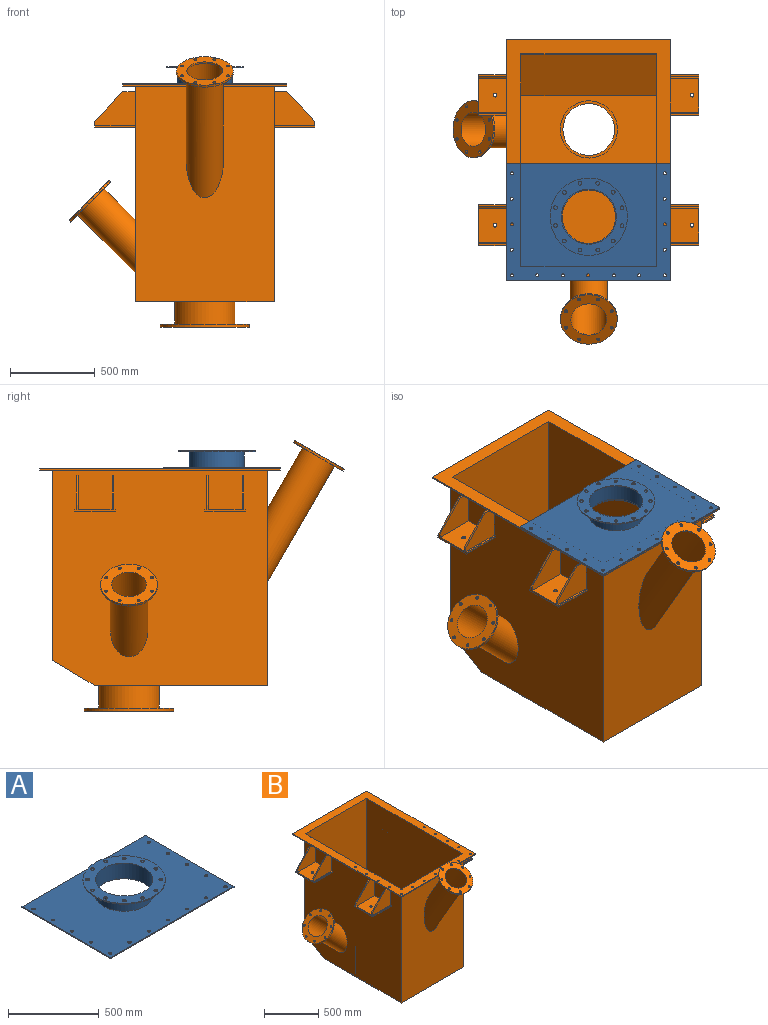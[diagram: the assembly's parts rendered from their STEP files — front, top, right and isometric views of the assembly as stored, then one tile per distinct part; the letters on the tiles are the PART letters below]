
ASSEMBLY  parts=2 mates=1
PART A: 38 faces, bbox 966x690x106 mm
  f0: cylinder r=161.9mm len=323.8mm, axis (0,0,-1), area 95621.3mm2, adj f20,f35
  f1: plane 966x6mm, normal (0,1,0), area 5796mm2, adj f2,f18,f20,f21
  f2: plane 690x6mm, normal (-1,0,0), area 4140mm2, adj f1,f3,f20,f21
  f3: plane 966x6mm, normal (0,-1,0), area 5796mm2, adj f2,f18,f20,f21
  f4: cylinder r=9mm len=18mm, axis (0,0,-1), area 339.3mm2, adj f20,f21
  f5: cylinder r=9mm len=18mm, axis (0,0,-1), area 339.3mm2, adj f20,f21
  f6: cylinder r=9mm len=18mm, axis (0,0,-1), area 339.3mm2, adj f20,f21
  f7: cylinder r=9mm len=18mm, axis (0,0,-1), area 339.3mm2, adj f20,f21
  f8: cylinder r=9mm len=18mm, axis (0,0,-1), area 339.3mm2, adj f20,f21
  f9: cylinder r=9mm len=18mm, axis (0,0,-1), area 339.3mm2, adj f20,f21
  f10: cylinder r=9mm len=18mm, axis (0,0,-1), area 339.3mm2, adj f20,f21
  f11: cylinder r=9mm len=18mm, axis (0,0,-1), area 339.3mm2, adj f20,f21
  f12: cylinder r=9mm len=18mm, axis (0,0,-1), area 339.3mm2, adj f20,f21
  f13: cylinder r=9mm len=18mm, axis (0,0,-1), area 339.3mm2, adj f20,f21
  f14: cylinder r=9mm len=18mm, axis (0,0,-1), area 339.3mm2, adj f20,f21
  f15: cylinder r=9mm len=18mm, axis (0,0,-1), area 339.3mm2, adj f20,f21
  f16: cylinder r=9mm len=18mm, axis (0,0,-1), area 339.3mm2, adj f20,f21
  f17: cylinder r=9mm len=18mm, axis (0,0,-1), area 339.3mm2, adj f20,f21
  f18: plane 690x6mm, normal (1,0,0), area 4140mm2, adj f1,f3,f20,f21
  f19: cylinder r=9mm len=18mm, axis (0,0,-1), area 339.3mm2, adj f20,f21
  f20: plane 966x690mm, normal (0,0,1), area 580376.8mm2, adj f0,f1,f2,f3,f4,f5,f6,f7
  f21: plane 966x690mm, normal (0,0,-1), area 584960mm2, adj f1,f2,f3,f4,f5,f6,f7,f8
  f22: cylinder r=11mm len=22mm, axis (0,0,1), area 414.7mm2, adj f35,f37
  f23: cylinder r=11mm len=22mm, axis (0,0,1), area 414.7mm2, adj f35,f37
  f24: cylinder r=11mm len=22mm, axis (0,0,1), area 414.7mm2, adj f35,f37
  f25: cylinder r=11mm len=22mm, axis (0,0,1), area 414.7mm2, adj f35,f37
  f26: cylinder r=11mm len=22mm, axis (0,0,1), area 414.7mm2, adj f35,f37
  f27: cylinder r=11mm len=22mm, axis (0,0,1), area 414.7mm2, adj f35,f37
  f28: cylinder r=11mm len=22mm, axis (0,0,1), area 414.7mm2, adj f35,f37
  f29: cylinder r=11mm len=22mm, axis (0,0,1), area 414.7mm2, adj f35,f37
  f30: cylinder r=11mm len=22mm, axis (0,0,1), area 414.7mm2, adj f35,f37
  f31: cylinder r=11mm len=22mm, axis (0,0,1), area 414.7mm2, adj f35,f37
  f32: cylinder r=11mm len=22mm, axis (0,0,1), area 414.7mm2, adj f35,f37
  f33: cylinder r=11mm len=22mm, axis (0,0,1), area 414.7mm2, adj f35,f37
  f34: cylinder r=227.5mm len=455mm, axis (0,0,1), area 8576.5mm2, adj f35,f37
  f35: plane 455x455mm, normal (0,0,-1), area 75689.3mm2, adj f0,f22,f23,f24,f25,f26,f27,f28
  f36: cylinder r=157.33mm len=314.66mm, axis (0,0,-1), area 104784.6mm2, adj f21,f37
  f37: plane 455x455mm, normal (0,0,1), area 80272.5mm2, adj f22,f23,f24,f25,f26,f27,f28,f29
PART B: 146 faces, bbox 1526.5x1870.7x1672 mm
  f0: plane 1269x1266mm, normal (-1,0,0), area 1521684.1mm2, adj f4,f6,f8,f9,f35,f99,f100,f101
  f1: cylinder r=109.55mm len=790.66mm, axis (0,-0.5,0.87), area 410746.3mm2, adj f6,f48
  f2: plane 800x415.78mm, normal (0,0,1), area 243673.8mm2, adj f3,f11,f14,f15,f37
  f3: plane 1269x1250mm, normal (-1,0,0), area 1562857.6mm2, adj f2,f7,f10,f12,f13,f14,f36,f37
  f4: plane 1119x816mm, normal (0,1,0), area 913104mm2, adj f0,f5,f9,f35
  f5: plane 1269x1266mm, normal (1,0,0), area 1575004mm2, adj f4,f6,f8,f9,f35,f69,f70,f71
  f6: plane 1348.81x895.81mm, normal (0,-1,0), area 960098.2mm2, adj f0,f1,f5,f8,f35
  f7: plane 1416x966mm, normal (0,0,1), area 364039mm2, adj f3,f10,f11,f12,f16,f17,f18,f19
  f8: plane 1016x816mm, normal (0,0,-1), area 729741.3mm2, adj f0,f5,f6,f9,f51
  f9: plane 816x250mm, normal (0,0.51,-0.86), area 237902.8mm2, adj f0,f4,f5,f8
  f10: plane 1122.47x800mm, normal (0,-1,0), area 897976.4mm2, adj f3,f7,f11,f14
  f11: plane 1269x1250mm, normal (1,0,0), area 1517203.1mm2, adj f2,f7,f10,f12,f13,f14,f36,f37
  f12: plane 1346.07x877.07mm, normal (0,1,0), area 944881.6mm2, adj f3,f7,f11,f13,f50
  f13: plane 800x580mm, normal (0,0,1), area 464000mm2, adj f3,f11,f12,f36
  f14: plane 800x244.22mm, normal (0,-0.51,0.86), area 227841.8mm2, adj f2,f3,f10,f11
  f15: cylinder r=168.27mm len=336.54mm, axis (0,0,-1), area 146960.8mm2, adj f2,f52
  f16: plane 1416x8mm, normal (1,0,0), area 11328mm2, adj f7,f17,f33,f35
  f17: plane 966x8mm, normal (0,1,0), area 7728mm2, adj f7,f16,f18,f35
  f18: plane 1416x8mm, normal (-1,0,0), area 11328mm2, adj f7,f17,f33,f35
  f19: cylinder r=9mm len=18mm, axis (0,0,1), area 452.4mm2, adj f7,f35
  f20: cylinder r=9mm len=18mm, axis (0,0,1), area 452.4mm2, adj f7,f35
  f21: cylinder r=9mm len=18mm, axis (0,0,1), area 452.4mm2, adj f7,f35
  f22: cylinder r=9mm len=18mm, axis (0,0,1), area 452.4mm2, adj f7,f35
  f23: cylinder r=9mm len=18mm, axis (0,0,1), area 452.4mm2, adj f7,f35
  f24: cylinder r=9mm len=18mm, axis (0,0,1), area 452.4mm2, adj f7,f35
  f25: cylinder r=9mm len=18mm, axis (0,0,1), area 452.4mm2, adj f7,f35
  f26: cylinder r=9mm len=18mm, axis (0,0,1), area 452.4mm2, adj f7,f35
  f27: cylinder r=9mm len=18mm, axis (0,0,1), area 452.4mm2, adj f7,f35
  f28: cylinder r=9mm len=18mm, axis (0,0,1), area 452.4mm2, adj f7,f35
  f29: cylinder r=9mm len=18mm, axis (0,0,1), area 452.4mm2, adj f7,f35
  f30: cylinder r=9mm len=18mm, axis (0,0,1), area 452.4mm2, adj f7,f35
  f31: cylinder r=9mm len=18mm, axis (0,0,1), area 452.4mm2, adj f7,f35
  f32: cylinder r=9mm len=18mm, axis (0,0,1), area 452.4mm2, adj f7,f35
  f33: plane 966x8mm, normal (0,-1,0), area 7728mm2, adj f7,f16,f18,f35
  f34: cylinder r=9mm len=18mm, axis (0,0,1), area 452.4mm2, adj f7,f35
  f35: plane 1416x966mm, normal (0,0,-1), area 330983mm2, adj f0,f4,f5,f6,f16,f17,f18,f19
  f36: plane 800x550mm, normal (0,-1,0), area 440000mm2, adj f3,f11,f13,f38
  f37: plane 800x550mm, normal (0,1,0), area 440000mm2, adj f2,f3,f11,f38
  f38: plane 800x10mm, normal (0,0,1), area 8000mm2, adj f3,f11,f36,f37
  f39: cylinder r=9mm len=22.09mm, axis (0,-0.5,0.87), area 735.1mm2, adj f48,f49
  f40: cylinder r=9mm len=22.09mm, axis (0,-0.5,0.87), area 735.1mm2, adj f48,f49
  f41: cylinder r=9mm len=22.09mm, axis (0,-0.5,0.87), area 735.1mm2, adj f48,f49
  f42: cylinder r=9mm len=22.09mm, axis (0,-0.5,0.87), area 735.1mm2, adj f48,f49
  f43: cylinder r=9mm len=22.09mm, axis (0,-0.5,0.87), area 735.1mm2, adj f48,f49
  f44: cylinder r=9mm len=22.09mm, axis (0,-0.5,0.87), area 735.1mm2, adj f48,f49
  f45: cylinder r=9mm len=22.09mm, axis (0,-0.5,0.87), area 735.1mm2, adj f48,f49
  f46: cylinder r=9mm len=22.09mm, axis (0,-0.5,0.87), area 735.1mm2, adj f48,f49
  f47: cylinder r=167.5mm len=335mm, axis (0,-0.5,0.87), area 13681.6mm2, adj f48,f49
  f48: plane 335x290.12mm, normal (0,0.5,-0.87), area 48402.7mm2, adj f1,f39,f40,f41,f42,f43,f44,f45
  f49: plane 335x290.12mm, normal (0,-0.5,0.87), area 50946.3mm2, adj f39,f40,f41,f42,f43,f44,f45,f46
  f50: cylinder r=105.79mm len=806.38mm, axis (0,-0.5,0.87), area 415924.9mm2, adj f12,f49
  f51: cylinder r=177.8mm len=355.6mm, axis (0,0,1), area 146346.7mm2, adj f8,f68
  f52: plane 336.54x336.54mm, normal (0,0,1), area 16016.4mm2, adj f15,f65
  f53: cylinder r=11mm len=22mm, axis (0,0,1), area 1313.2mm2, adj f67,f68
  f54: cylinder r=11mm len=22mm, axis (0,0,1), area 1313.2mm2, adj f67,f68
  f55: cylinder r=11mm len=22mm, axis (0,0,1), area 1313.2mm2, adj f67,f68
  f56: cylinder r=11mm len=22mm, axis (0,0,1), area 1313.2mm2, adj f67,f68
  f57: cylinder r=11mm len=22mm, axis (0,0,1), area 1313.2mm2, adj f67,f68
  f58: cylinder r=11mm len=22mm, axis (0,0,1), area 1313.2mm2, adj f67,f68
  f59: cylinder r=11mm len=22mm, axis (0,0,1), area 1313.2mm2, adj f67,f68
  f60: cylinder r=11mm len=22mm, axis (0,0,1), area 1313.2mm2, adj f67,f68
  f61: cylinder r=11mm len=22mm, axis (0,0,1), area 1313.2mm2, adj f67,f68
  f62: cylinder r=11mm len=22mm, axis (0,0,1), area 1313.2mm2, adj f67,f68
  f63: cylinder r=11mm len=22mm, axis (0,0,1), area 1313.2mm2, adj f67,f68
  f64: cylinder r=11mm len=22mm, axis (0,0,1), area 1313.2mm2, adj f67,f68
  f65: cylinder r=152.37mm len=304.74mm, axis (0,0,1), area 18190mm2, adj f52,f67
  f66: cylinder r=262.5mm len=525mm, axis (0,0,1), area 31337.4mm2, adj f67,f68
  f67: plane 525x525mm, normal (0,0,-1), area 138976.6mm2, adj f53,f54,f55,f56,f57,f58,f59,f60
  f68: plane 525x525mm, normal (0,0,1), area 112599.1mm2, adj f51,f53,f54,f55,f56,f57,f58,f59
  f69: plane 240x200mm, normal (0,-1,0), area 33562.5mm2, adj f5,f74,f75,f76,f82
  f70: plane 75x10mm, normal (0,0,1), area 750mm2, adj f5,f71,f72,f83
  f71: plane 240x200mm, normal (0,1,0), area 33562.5mm2, adj f5,f70,f74,f80,f83
  f72: plane 240x200mm, normal (0,-1,0), area 33562.5mm2, adj f5,f70,f74,f81,f83
  f73: plane 240x200mm, normal (0,1,0), area 33562.5mm2, adj f5,f74,f75,f81,f82
  f74: plane 240x35mm, normal (1,0,0), area 2900mm2, adj f69,f71,f72,f73,f76,f77,f78,f79
  f75: plane 75x10mm, normal (0,0,1), area 750mm2, adj f5,f69,f73,f82
  f76: plane 240x10mm, normal (0,0,1), area 2400mm2, adj f5,f69,f74,f77
  f77: plane 240x10mm, normal (0,-1,0), area 2400mm2, adj f5,f74,f76,f78
  f78: plane 240x240mm, normal (0,0,-1), area 57219.9mm2, adj f5,f74,f77,f79,f132
  f79: plane 240x10mm, normal (0,1,0), area 2400mm2, adj f5,f74,f78,f80
  f80: plane 240x10mm, normal (0,0,1), area 2400mm2, adj f5,f71,f74,f79
  f81: plane 240x200mm, normal (0,0,1), area 47619.9mm2, adj f5,f72,f73,f74,f132
  f82: plane 175x165mm, normal (0.73,0,0.69), area 2405.2mm2, adj f69,f73,f74,f75
  f83: plane 175x165mm, normal (0.73,0,0.69), area 2405.2mm2, adj f70,f71,f72,f74
  f84: plane 75x10mm, normal (0,0,1), area 750mm2, adj f5,f85,f86,f98
  f85: plane 240x200mm, normal (0,1,0), area 33562.5mm2, adj f5,f84,f89,f90,f98
  f86: plane 240x200mm, normal (0,-1,0), area 33562.5mm2, adj f5,f84,f89,f91,f98
  f87: plane 240x200mm, normal (0,1,0), area 33562.5mm2, adj f5,f89,f91,f92,f97
  f88: plane 240x200mm, normal (0,-1,0), area 33562.5mm2, adj f5,f89,f92,f93,f97
  f89: plane 240x35mm, normal (1,0,0), area 2900mm2, adj f85,f86,f87,f88,f90,f91,f93,f94
  f90: plane 240x10mm, normal (0,0,1), area 2400mm2, adj f5,f85,f89,f96
  f91: plane 240x200mm, normal (0,0,1), area 47619.9mm2, adj f5,f86,f87,f89,f131
  f92: plane 75x10mm, normal (0,0,1), area 750mm2, adj f5,f87,f88,f97
  f93: plane 240x10mm, normal (0,0,1), area 2400mm2, adj f5,f88,f89,f94
  f94: plane 240x10mm, normal (0,-1,0), area 2400mm2, adj f5,f89,f93,f95
  f95: plane 240x240mm, normal (0,0,-1), area 57219.9mm2, adj f5,f89,f94,f96,f131
  f96: plane 240x10mm, normal (0,1,0), area 2400mm2, adj f5,f89,f90,f95
  f97: plane 175x165mm, normal (0.73,0,0.69), area 2405.2mm2, adj f87,f88,f89,f92
  f98: plane 175x165mm, normal (0.73,0,0.69), area 2405.2mm2, adj f84,f85,f86,f89
  f99: plane 240x200mm, normal (0,-1,0), area 33562.5mm2, adj f0,f104,f105,f106,f112
  f100: plane 75x10mm, normal (0,0,1), area 750mm2, adj f0,f101,f102,f113
  f101: plane 240x200mm, normal (0,1,0), area 33562.5mm2, adj f0,f100,f104,f110,f113
  f102: plane 240x200mm, normal (0,-1,0), area 33562.5mm2, adj f0,f100,f104,f111,f113
  f103: plane 240x200mm, normal (0,1,0), area 33562.5mm2, adj f0,f104,f105,f111,f112
  f104: plane 240x35mm, normal (-1,0,0), area 2900mm2, adj f99,f101,f102,f103,f106,f107,f108,f109
  f105: plane 75x10mm, normal (0,0,1), area 750mm2, adj f0,f99,f103,f112
  f106: plane 240x10mm, normal (0,0,1), area 2400mm2, adj f0,f99,f104,f107
  f107: plane 240x10mm, normal (0,-1,0), area 2400mm2, adj f0,f104,f106,f108
  f108: plane 240x240mm, normal (0,0,-1), area 57219.9mm2, adj f0,f104,f107,f109,f130
  f109: plane 240x10mm, normal (0,1,0), area 2400mm2, adj f0,f104,f108,f110
  f110: plane 240x10mm, normal (0,0,1), area 2400mm2, adj f0,f101,f104,f109
  f111: plane 240x200mm, normal (0,0,1), area 47619.9mm2, adj f0,f102,f103,f104,f130
  f112: plane 175x165mm, normal (-0.73,0,0.69), area 2405.2mm2, adj f99,f103,f104,f105
  f113: plane 175x165mm, normal (-0.73,0,0.69), area 2405.2mm2, adj f100,f101,f102,f104
  f114: plane 75x10mm, normal (0,0,1), area 750mm2, adj f0,f115,f116,f128
  f115: plane 240x200mm, normal (0,1,0), area 33562.5mm2, adj f0,f114,f119,f120,f128
  f116: plane 240x200mm, normal (0,-1,0), area 33562.5mm2, adj f0,f114,f119,f121,f128
  f117: plane 240x200mm, normal (0,1,0), area 33562.5mm2, adj f0,f119,f121,f122,f127
  f118: plane 240x200mm, normal (0,-1,0), area 33562.5mm2, adj f0,f119,f122,f123,f127
  f119: plane 240x35mm, normal (-1,0,0), area 2900mm2, adj f115,f116,f117,f118,f120,f121,f123,f124
  f120: plane 240x10mm, normal (0,0,1), area 2400mm2, adj f0,f115,f119,f126
  f121: plane 240x200mm, normal (0,0,1), area 47619.9mm2, adj f0,f116,f117,f119,f129
  f122: plane 75x10mm, normal (0,0,1), area 750mm2, adj f0,f117,f118,f127
  f123: plane 240x10mm, normal (0,0,1), area 2400mm2, adj f0,f118,f119,f124
  f124: plane 240x10mm, normal (0,-1,0), area 2400mm2, adj f0,f119,f123,f125
  f125: plane 240x240mm, normal (0,0,-1), area 57219.9mm2, adj f0,f119,f124,f126,f129
  f126: plane 240x10mm, normal (0,1,0), area 2400mm2, adj f0,f119,f120,f125
  f127: plane 175x165mm, normal (-0.73,0,0.69), area 2405.2mm2, adj f117,f118,f119,f122
  f128: plane 175x165mm, normal (-0.73,0,0.69), area 2405.2mm2, adj f114,f115,f116,f119
  f129: cylinder r=11mm len=22mm, axis (0,0,-1), area 691.2mm2, adj f121,f125
  f130: cylinder r=11mm len=22mm, axis (0,0,-1), area 691.2mm2, adj f108,f111
  f131: cylinder r=11mm len=22mm, axis (0,0,-1), area 691.2mm2, adj f91,f95
  f132: cylinder r=11mm len=22mm, axis (0,0,-1), area 691.2mm2, adj f78,f81
  f133: cylinder r=101.37mm len=496.28mm, axis (-0.71,0,0.71), area 252443.4mm2, adj f11,f135
  f134: cylinder r=109.55mm len=496.52mm, axis (-0.71,0,0.71), area 256078.4mm2, adj f0,f145
  f135: plane 335x236.88mm, normal (-0.71,0,0.71), area 53822.9mm2, adj f133,f136,f137,f138,f139,f140,f141,f142
  f136: cylinder r=9mm len=21.92mm, axis (-0.71,0,0.71), area 735.1mm2, adj f135,f145
  f137: cylinder r=9mm len=21.92mm, axis (-0.71,0,0.71), area 735.1mm2, adj f135,f145
  f138: cylinder r=9mm len=21.92mm, axis (-0.71,0,0.71), area 735.1mm2, adj f135,f145
  f139: cylinder r=9mm len=21.92mm, axis (-0.71,0,0.71), area 735.1mm2, adj f135,f145
  f140: cylinder r=9mm len=21.92mm, axis (-0.71,0,0.71), area 735.1mm2, adj f135,f145
  f141: cylinder r=9mm len=21.92mm, axis (-0.71,0,0.71), area 735.1mm2, adj f135,f145
  f142: cylinder r=9mm len=21.92mm, axis (-0.71,0,0.71), area 735.1mm2, adj f135,f145
  f143: cylinder r=9mm len=21.92mm, axis (-0.71,0,0.71), area 735.1mm2, adj f135,f145
  f144: cylinder r=167.5mm len=335mm, axis (-0.71,0,0.71), area 13681.6mm2, adj f135,f145
  f145: plane 335x236.88mm, normal (0.71,0,-0.71), area 48402.7mm2, adj f134,f136,f137,f138,f139,f140,f141,f142
PLACE A t=(-127,5.05,-834.6)mm
PLACE B t=(-127,5.05,-834.6)mm
MATE revolute A.f13 <-> B.f20  axis (0,0,-1) through (-580,-672.95,573.4)mm
